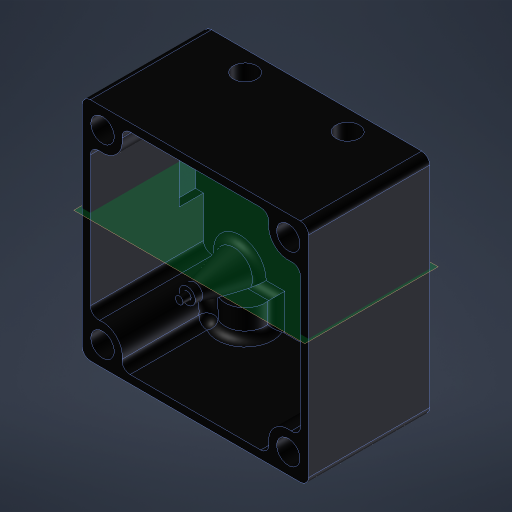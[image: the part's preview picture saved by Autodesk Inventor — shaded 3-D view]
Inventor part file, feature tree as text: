
AUTODESK INVENTOR PART (.ipt)
format: ipt  version: 2023 (Build 270158000, 158)  size: 531,968 bytes
history: native  units: in
note: dims shown in document units (in); Inventor stores cm internally (conversion verified against a paired STEP export)
features: sketch x6, extrude x6, projected_geometry x4, fillet x2, chamfer x2, hole x1, mirror x1, shell x1, plane x1
ambient origin geometry x8: Origin, YZ Plane, XZ Plane, XY Plane, X Axis, Y Axis, Z Axis, Center Point
bodies: Solid1 (feature_tree)
feature tree (24):
  sketch  "Sketch1"  dims[d0=1.4961in d1=1.4961in]
  extrude  "Extrusion1"  Depth=1.4961in
  hole  "Hole1"  [1 undecoded]
  extrude  "Extrusion6"  Depth=0.0787in
  mirror  "Mirror1"
  shell  "Shell1"  Thickness=0.3937in
  fillet  "Fillet1"  Radius=1.811in
  extrude  "Extrusion2"  Depth=0.0787in
  chamfer  "Chamfer1"  Distance=0.1575in
  extrude  "Extrusion3"  Depth=0.0787in
  sketch  "Sketch3"  dims[d5=1.1811in d6=0.0in d7=0.0787in d8=0.3937in d9=1.811in]
  extrude  "Extrusion4"  Depth=0.0787in TaperAngle=0.0deg
  plane  "Work Plane1"
  extrude  "Extrusion5"  Depth=0.0787in TaperAngle=75.0deg
  chamfer  "Chamfer2"  Distance=0.0748in
  fillet  "Fillet3"  Radius=0.0748in
  sketch  "Sketch2"  dims[d2=1.3386in d3=1.3386in]
  projected_geometry  "Projected Loop1"
  projected_geometry  "Projected Loop2"
  projected_geometry  "Projected Loop3"
  sketch  "Sketch4"  dims[d10=0.2283in d11=0.2362in d12=0.385in d13=0.0787in d14=0.5635in d15=0.315in d16=0.8108in d17=0.0787in]
  sketch  "Sketch5"  dims[d18=0.1575in]
  sketch  "Sketch6"  dims[d19=0.1575in d20=0.1575in d21=0.1575in d22=0.5906in d23=0.0in d24=0.1181in d25=0.0787in d26=75.0deg d27=0.0748in d28=0.0748in d29=0.0748in d30=0.0748in d31=0.0787in d32=0.0in d33=0.4724in d34=0.2362in d35=0.0787in d36=1.1811in d37=0.0in d38=-1.25in d39=45.0deg d40=0.1969in d41=0.0787in d42=0.1969in d43=0.0in d44=0.0197in d45=0.0787in d46=0.481in d47=0.2283in d48=0.2283in d49=0.1969in d50=1.0in d51=0.2756in d52=0.0in d61=0.0787in d60=0.0in d62=0.0in d63=0.0in]
  projected_geometry  "Project Cut Edges1"
note: 1 required parameter value undecoded (feature->parameter linkage not recoverable at this tier; creation-order binding heuristic only, values carry confidence <= 0.55)
